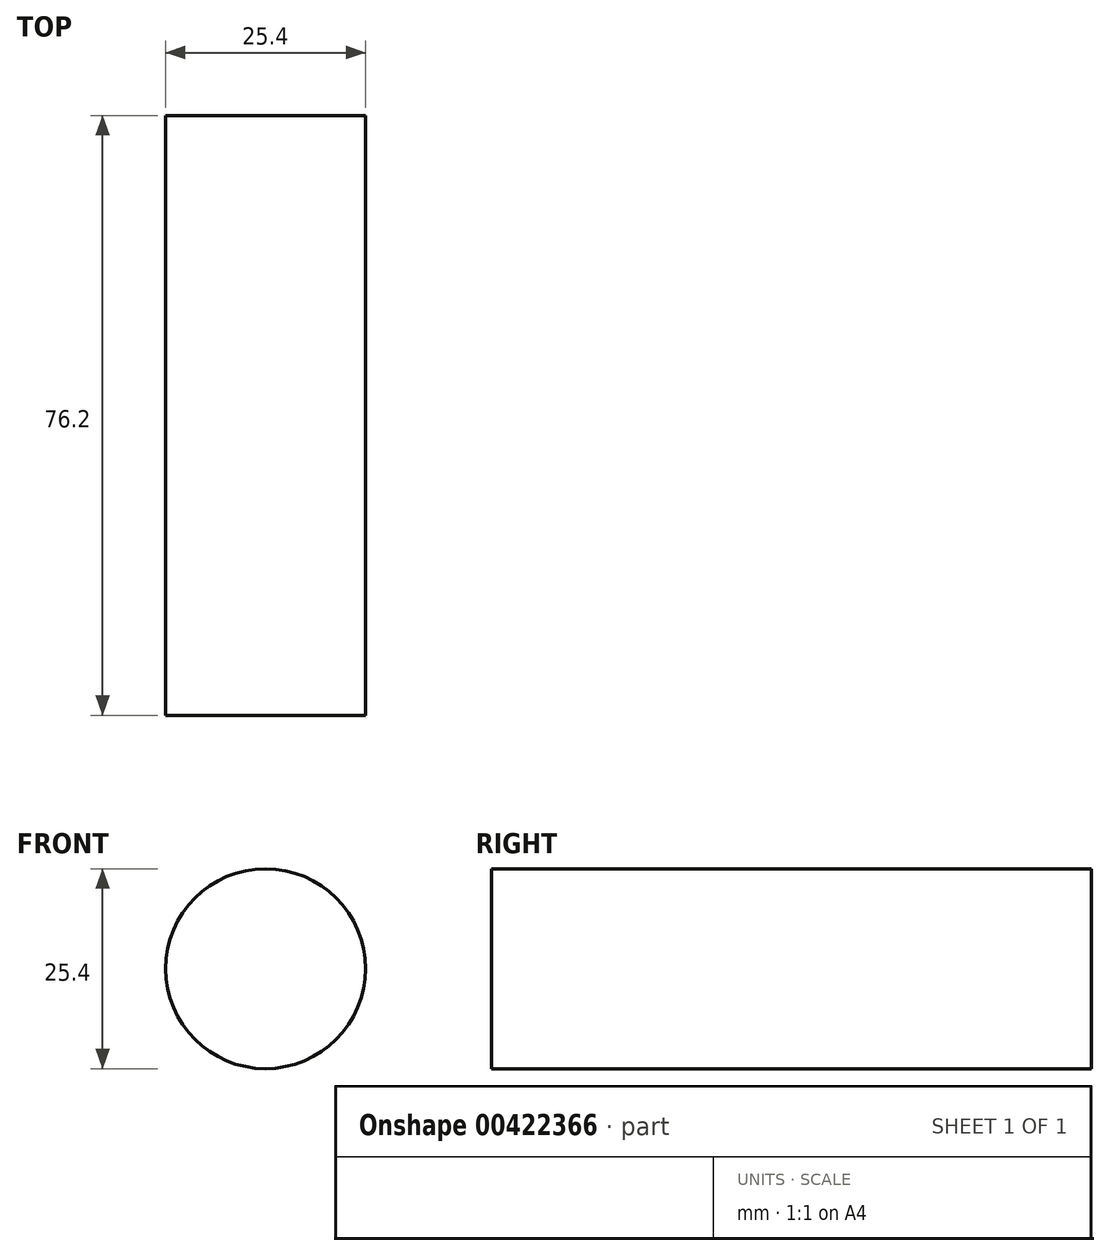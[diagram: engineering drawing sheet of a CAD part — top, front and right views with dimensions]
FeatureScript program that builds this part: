
annotation { "Feature Type Name" : "Feature", "Feature Type Description" : "" }
export const myFeature = defineFeature(function(context is Context, id is Id, definition is map)
    precondition{}
    {
        {
            var Q0;
            Q0=qCreatedBy(makeId("Front.planeOp"),FACE);
            var sketch = newSketch(context, id + "F0", { "sketchPlane" : qUnion([Q0])});
            skCircle(sketch, "E0", {"center": v(-28.83, 6.3) * mm, "radius": 12.7 * mm});
            skSolve(sketch);
        }
        {
            var Q0;
            Q0 = qSketchRegion(id + "F0", true);
            extrude(context, id + "F1", {"entities" : qUnion([Q0]), "depth" : 76.2 * mm});
        }
    });
